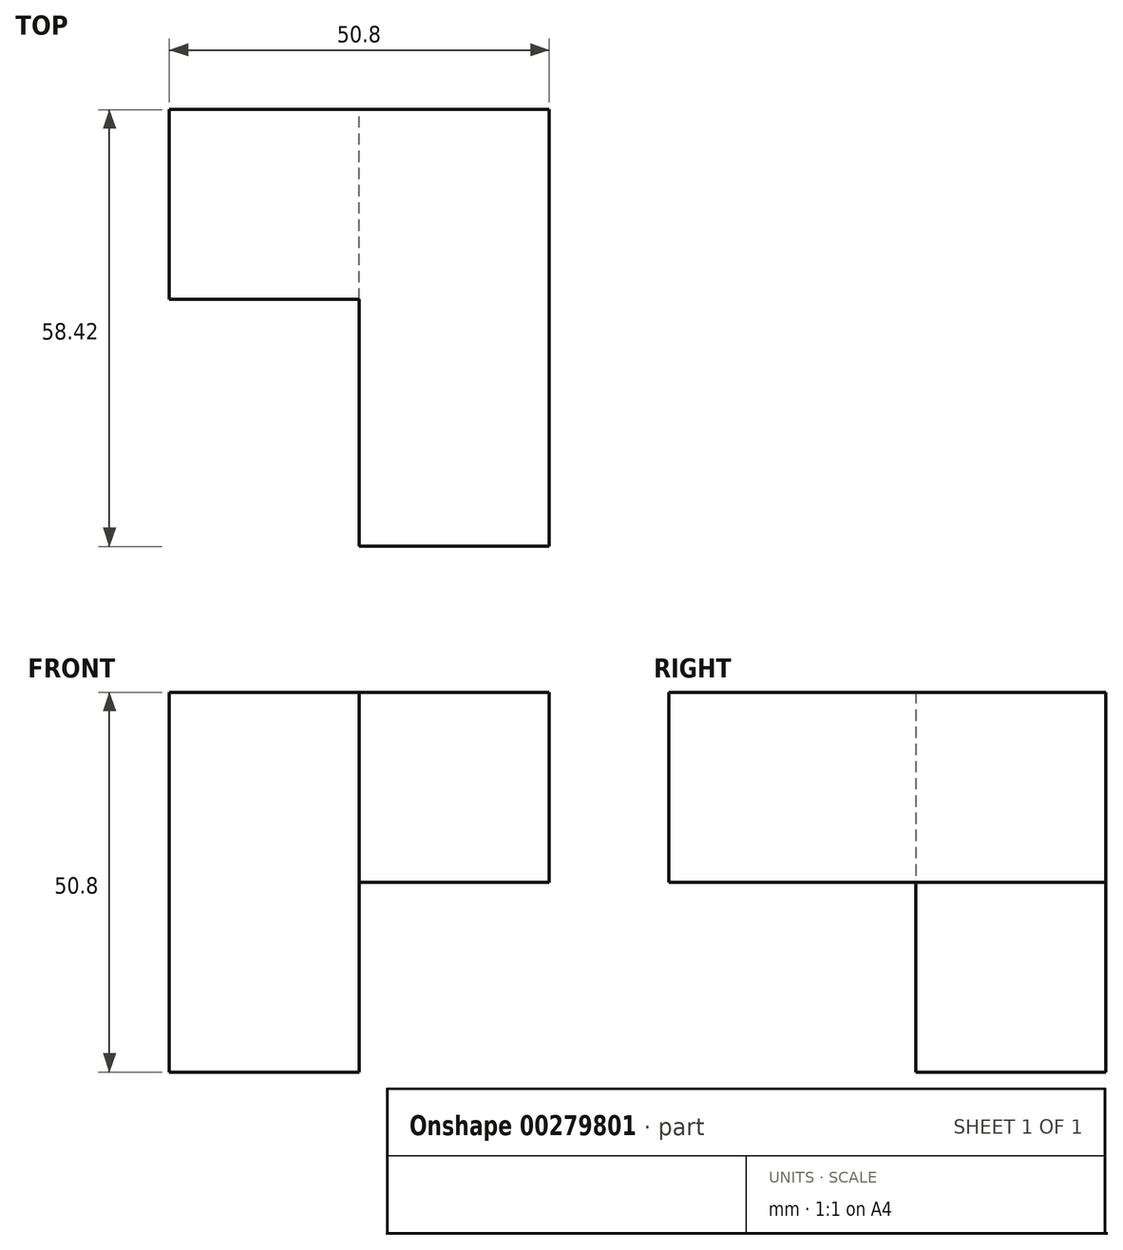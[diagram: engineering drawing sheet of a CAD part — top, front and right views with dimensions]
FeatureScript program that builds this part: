
annotation { "Feature Type Name" : "Feature", "Feature Type Description" : "" }
export const myFeature = defineFeature(function(context is Context, id is Id, definition is map)
    precondition{}
    {
        {
            var Q0;
            Q0=qCreatedBy(makeId("Right.planeOp"),FACE);
            var sketch = newSketch(context, id + "F0", { "sketchPlane" : qUnion([Q0])});
            skLineSegment(sketch, "E0.bottom", {"start": v(-4.58, 29.85) * mm, "end": v(-63, 29.85) * mm});
            skLineSegment(sketch, "E0.top", {"start": v(-4.58, 4.45) * mm, "end": v(-63, 4.45) * mm});
            skLineSegment(sketch, "E0.left", {"start": v(-4.58, 29.85) * mm, "end": v(-4.58, 4.45) * mm});
            skLineSegment(sketch, "E0.right", {"start": v(-63, 29.85) * mm, "end": v(-63, 4.45) * mm});
            skSolve(sketch);
        }
        {
            var Q0;
            Q0=makeQuery(id+"F0.imprint","IMPRINT",FACE,{"disambiguationData":[TD([[makeQuery(id+"F0.imprint","IMPRINT",EDGE,{"derivedFrom":sQuery(id+"F0.wireOp",EDGE,"E0.bottom")}),1.0]])]});
            extrude(context, id + "F1", {"entities" : qUnion([Q0]), "depth" : 25.4 * mm});
        }
        {
            var Q0;
            Q0=makeQuery(id+"F1.opExtrude","CAP_FACE",FACE,{"disambiguationData":[OSD([sQuery(id+"F0.wireOp",EDGE,"E0.bottom"),sQuery(id+"F0.wireOp",EDGE,"E0.top"),sQuery(id+"F0.wireOp",EDGE,"E0.left"),sQuery(id+"F0.wireOp",EDGE,"E0.right")])],"isStart":true});
            var sketch = newSketch(context, id + "F2", { "sketchPlane" : qUnion([Q0])});
            skLineSegment(sketch, "E1", {"start": v(29.98, 29.85) * mm, "end": v(29.98, 4.45) * mm});
            skSolve(sketch);
        }
        {
            var Q0;
            {var subQ0=sQuery(id+"F2.wireOp",EDGE,"E1");Q0=makeQuery(id+"F2.imprint","IMPRINT",FACE,{"disambiguationData":[TD([[makeQuery(id+"F2.imprint","IMPRINT",EDGE,{"derivedFrom":subQ0}),-1.0]])]});}
            extrude(context, id + "F3", {"entities" : qUnion([Q0]), "operationType" : NewBodyOperationType.ADD, "depth" : 25.4 * mm});
        }
        {
            var Q0;
            {var subQ0=sQuery(id+"F0.wireOp",EDGE,"E0.top");Q0=makeQuery(id+"F3.boolean.opBoolean","MERGE",FACE,{"derivedFrom":[makeQuery(id+"F1.opExtrude","SWEPT_FACE",FACE,{"disambiguationData":[OSD([subQ0])]}),makeQuery(id+"F3.opExtrude","SWEPT_FACE",FACE,{"disambiguationData":[OSD([subQ0])]})]});}
            var sketch = newSketch(context, id + "F4", { "sketchPlane" : qUnion([Q0])});
            skLineSegment(sketch, "E2", {"start": v(0, 29.98) * mm, "end": v(0, 4.58) * mm});
            skSolve(sketch);
        }
        {
            var Q0;
            {var subQ0=sQuery(id+"F4.wireOp",EDGE,"E2");Q0=makeQuery(id+"F4.imprint","IMPRINT",FACE,{"disambiguationData":[TD([[makeQuery(id+"F4.imprint","IMPRINT",EDGE,{"derivedFrom":subQ0}),-1.0]])]});}
            extrude(context, id + "F5", {"entities" : qUnion([Q0]), "operationType" : NewBodyOperationType.ADD, "depth" : 25.4 * mm});
        }
    });
